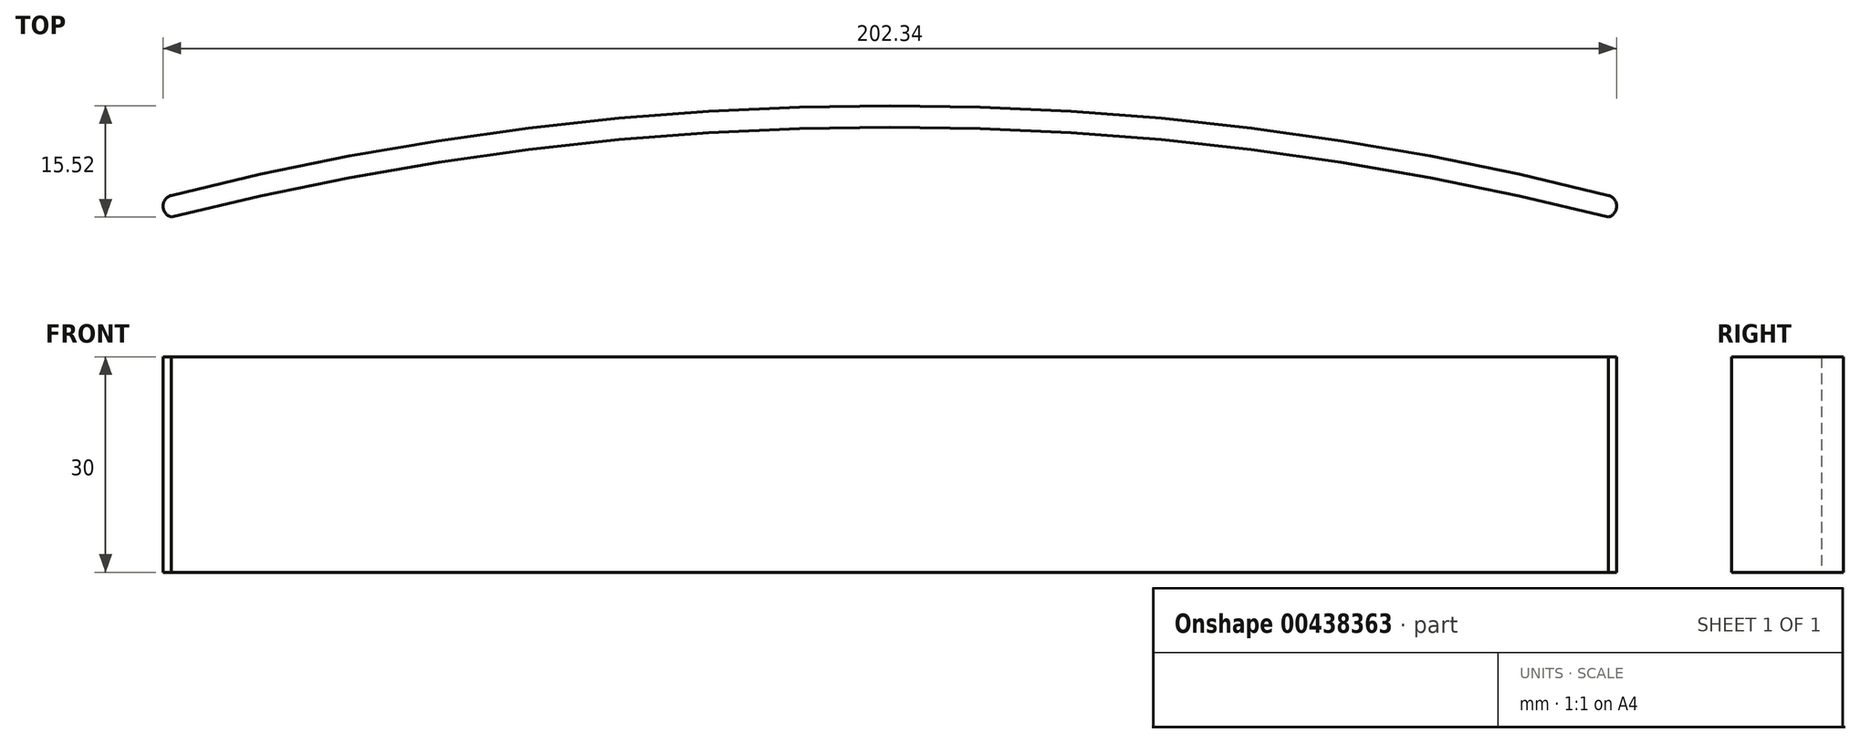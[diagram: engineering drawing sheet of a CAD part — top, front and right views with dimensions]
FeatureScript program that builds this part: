
annotation { "Feature Type Name" : "Feature", "Feature Type Description" : "" }
export const myFeature = defineFeature(function(context is Context, id is Id, definition is map)
    precondition{}
    {
        {
            var Q0;
            Q0=qCreatedBy(makeId("Top.planeOp"),FACE);
            var sketch = newSketch(context, id + "F0", { "sketchPlane" : qUnion([Q0])});
            skArc(sketch, "E0", {"start": v(99.44, 0) * mm, "mid": v(-0.56, 12.52) * mm, "end": v(-100.56, 0) * mm});
            skArc(sketch, "E1", {"start": v(99.44, 3) * mm, "mid": v(-0.56, 15.52) * mm, "end": v(-100.56, 3) * mm});
            skArc(sketch, "E2", {"start": v(-100.56, 3) * mm, "mid": v(-101.73, 1.5) * mm, "end": v(-100.56, 0) * mm});
            skArc(sketch, "E3", {"start": v(99.44, 3) * mm, "mid": v(100.6, 1.5) * mm, "end": v(99.44, 0) * mm});
            skSolve(sketch);
        }
        {
            var Q0;
            Q0=makeQuery(id+"F0.imprint","IMPRINT",FACE,{"disambiguationData":[TD([[makeQuery(id+"F0.imprint","IMPRINT",EDGE,{"derivedFrom":sQuery(id+"F0.wireOp",EDGE,"E0")}),-1.0]])]});
            extrude(context, id + "F1", {"entities" : qUnion([Q0]), "depth" : 30 * mm});
        }
    });
